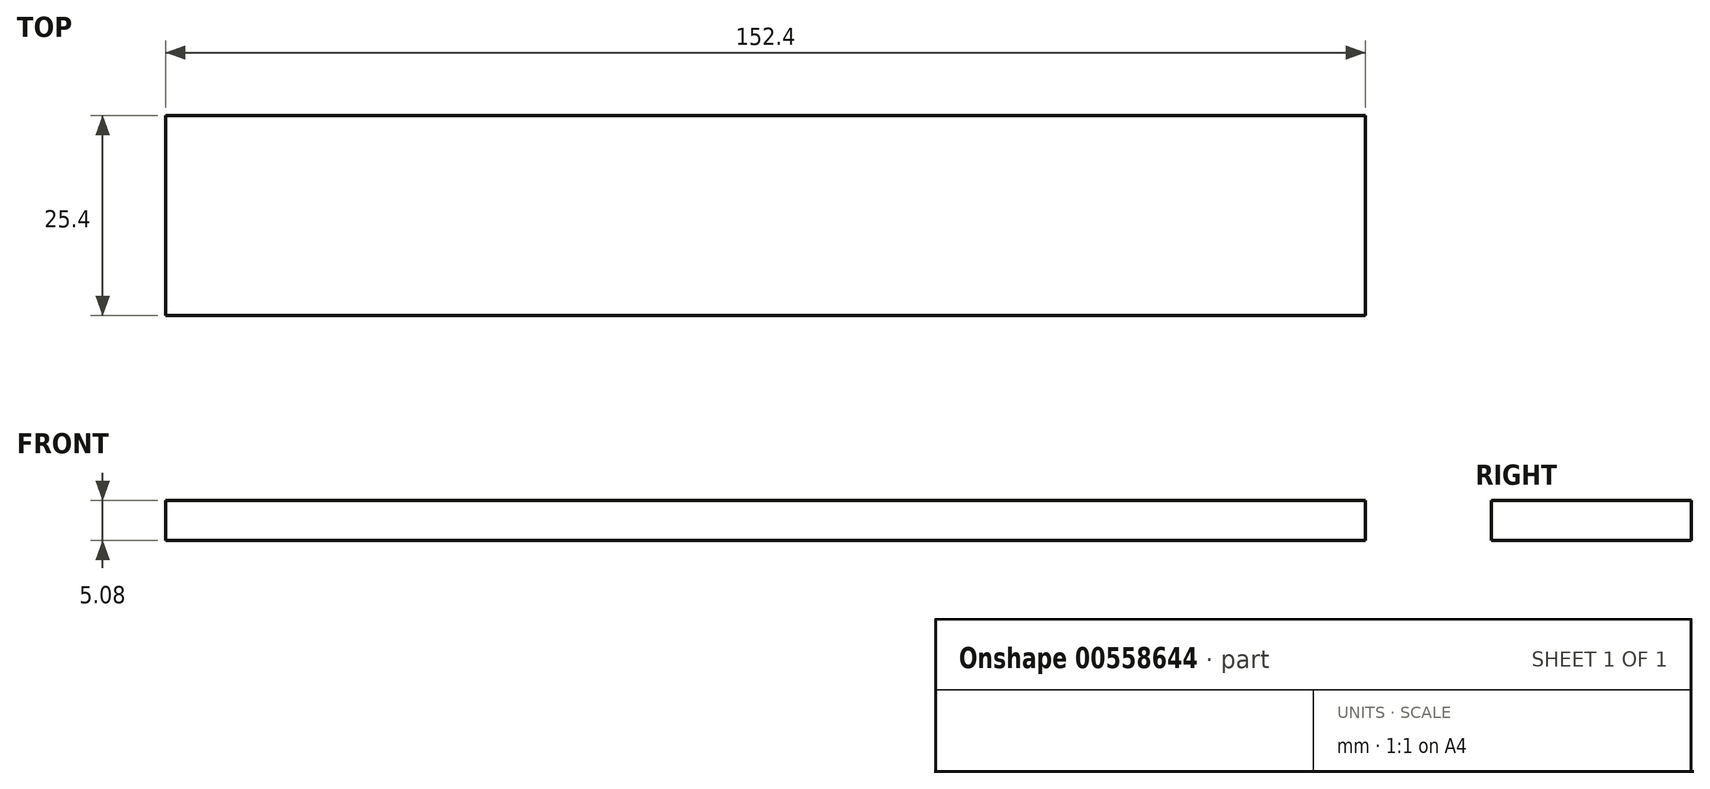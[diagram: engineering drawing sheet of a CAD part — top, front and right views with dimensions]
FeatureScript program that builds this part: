
annotation { "Feature Type Name" : "Feature", "Feature Type Description" : "" }
export const myFeature = defineFeature(function(context is Context, id is Id, definition is map)
    precondition{}
    {
        {
            var Q0;
            Q0=qCreatedBy(makeId("Top.planeOp"),FACE);
            var sketch = newSketch(context, id + "F0", { "sketchPlane" : qUnion([Q0])});
            skLineSegment(sketch, "E0.bottom", {"start": v(0, 0) * mm, "end": v(152.4, 0) * mm});
            skLineSegment(sketch, "E0.top", {"start": v(0, 25.4) * mm, "end": v(152.4, 25.4) * mm});
            skLineSegment(sketch, "E0.left", {"start": v(0, 0) * mm, "end": v(0, 25.4) * mm});
            skLineSegment(sketch, "E0.right", {"start": v(152.4, 0) * mm, "end": v(152.4, 25.4) * mm});
            skSolve(sketch);
        }
        {
            var Q0;
            Q0=makeQuery(id+"F0.imprint","IMPRINT",FACE,{"disambiguationData":[TD([[makeQuery(id+"F0.imprint","IMPRINT",EDGE,{"derivedFrom":sQuery(id+"F0.wireOp",EDGE,"E0.bottom")}),1.0]])]});
            extrude(context, id + "F1", {"entities" : qUnion([Q0]), "depth" : 5.08 * mm, "offsetDistance" : 25.4 * mm});
        }
    });
